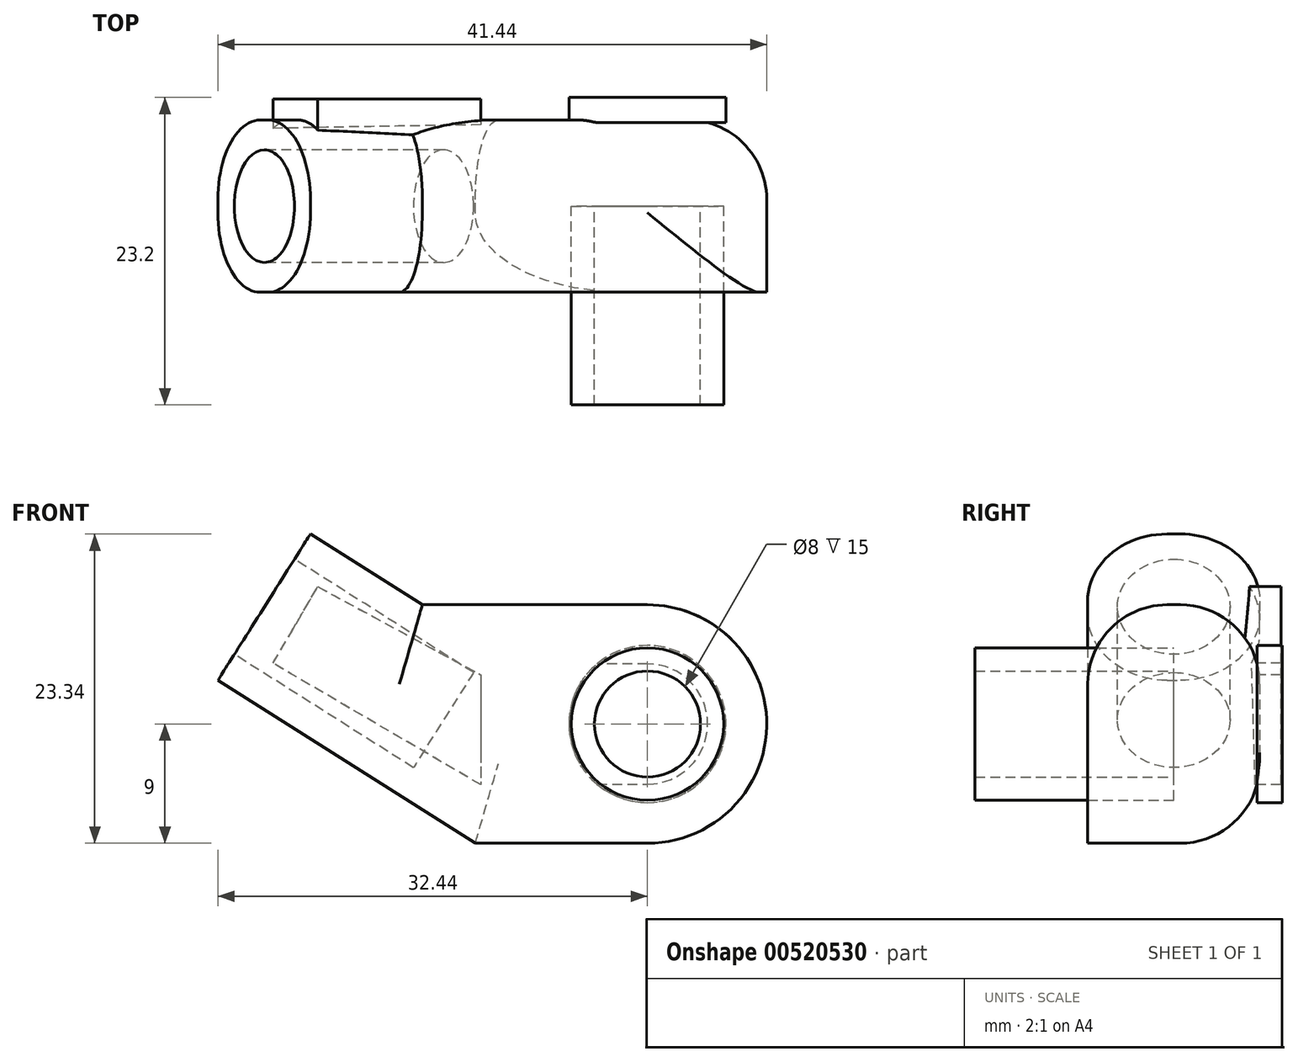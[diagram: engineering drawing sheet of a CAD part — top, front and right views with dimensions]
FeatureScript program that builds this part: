
annotation { "Feature Type Name" : "Feature", "Feature Type Description" : "" }
export const myFeature = defineFeature(function(context is Context, id is Id, definition is map)
    precondition{}
    {
        {
            var Q0;
            Q0=qCreatedBy(makeId("Front.planeOp"),FACE);
            var sketch = newSketch(context, id + "F0", { "sketchPlane" : qUnion([Q0])});
            skCircle(sketch, "E0", {"center": v(0, 0) * mm, "radius": 9 * mm});
            skLineSegment(sketch, "E1", {"start": v(0, -9) * mm, "end": v(-13, -9) * mm});
            skLineSegment(sketch, "E2", {"start": v(-13, -9) * mm, "end": v(-32.44, 3.3) * mm});
            skLineSegment(sketch, "E3", {"start": v(-32.44, 3.3) * mm, "end": v(-25.45, 14.34) * mm});
            skLineSegment(sketch, "E4", {"start": v(-25.45, 14.34) * mm, "end": v(-17, 9) * mm});
            skLineSegment(sketch, "E5", {"start": v(-17, 9) * mm, "end": v(0, 9) * mm});
            skSolve(sketch);
        }
        {
            var Q0;
            {var subQ0=sQuery(id+"F0.wireOp",EDGE,"E1");Q0=makeQuery(id+"F0.imprint","IMPRINT",FACE,{"disambiguationData":[TD([[makeQuery(id+"F0.imprint","IMPRINT",EDGE,{"derivedFrom":subQ0}),-1.0]])]});}
            var Q1;
            {var subQ0=sQuery(id+"F0.wireOp",EDGE,"E0");var subQ1=makeQuery(id+"F0.imprint","INTERSECT",VERTEX,{"derivedFrom":[subQ0,sQuery(id+"F0.wireOp",EDGE,"E1")]});Q1=makeQuery(id+"F0.imprint","IMPRINT",FACE,{"disambiguationData":[TD([[makeQuery(id+"F0.imprint","IMPRINT",EDGE,{"disambiguationData":[TD([[subQ1,1.0]])],"derivedFrom":subQ0}),1.0]])]});}
            extrude(context, id + "F1", {"entities" : qUnion([Q0, Q1]), "endBound" : BoundingType.SYMMETRIC, "depth" : 13 * mm});
        }
        {
            var Q0;
            Q0=makeQuery(id+"F1.opExtrude","SWEPT_FACE",FACE,{"disambiguationData":[OSD([sQuery(id+"F0.wireOp",EDGE,"E3")])]});
            var sketch = newSketch(context, id + "F2", { "sketchPlane" : qUnion([Q0])});
            skCircle(sketch, "E6", {"center": v(0, -7.98) * mm, "radius": 4.25 * mm});
            skSolve(sketch);
        }
        {
            var Q0;
            Q0=qSketchRegion(id+"F2",true);
            extrude(context, id + "F3", {"entities" : qUnion([Q0]), "operationType" : NewBodyOperationType.REMOVE, "oppositeDirection" : true, "depth" : 16 * mm});
        }
        {
            var Q0;
            Q0=makeQuery(id+"F1.opExtrude","CAP_EDGE",EDGE,{"disambiguationData":[OSD([sQuery(id+"F0.wireOp",EDGE,"E4")])],"isStart":true});
            var Q1;
            Q1=makeQuery(id+"F1.opExtrude","CAP_EDGE",EDGE,{"disambiguationData":[OSD([sQuery(id+"F0.wireOp",EDGE,"E5")])],"isStart":true});
            var Q2;
            Q2=makeQuery(id+"F1.opExtrude","CAP_EDGE",EDGE,{"disambiguationData":[OSD([sQuery(id+"F0.wireOp",EDGE,"E2")])],"isStart":true});
            fillet(context, id + "F4", {"entities" : qUnion([Q0, Q1, Q2]), "radius" : 6 * mm, "tangentPropagation" : true, "allowEdgeOverflow" : false});
        }
        {
            var Q0;
            Q0=makeQuery(id+"F1.opExtrude","CAP_EDGE",EDGE,{"disambiguationData":[OSD([sQuery(id+"F0.wireOp",EDGE,"E4")])],"isStart":false});
            var Q1;
            Q1=makeQuery(id+"F1.opExtrude","CAP_EDGE",EDGE,{"disambiguationData":[OSD([sQuery(id+"F0.wireOp",EDGE,"E5")])],"isStart":false});
            var Q2;
            Q2=makeQuery(id+"F1.opExtrude","CAP_EDGE",EDGE,{"disambiguationData":[OSD([sQuery(id+"F0.wireOp",EDGE,"E2")])],"isStart":false});
            fillet(context, id + "F5", {"entities" : qUnion([Q0, Q1, Q2]), "radius" : 6 * mm, "allowEdgeOverflow" : false});
        }
        {
            var Q0;
            Q0=qCreatedBy(makeId("Front.planeOp"),FACE);
            var sketch = newSketch(context, id + "F6", { "sketchPlane" : qUnion([Q0])});
            skCircle(sketch, "E7", {"center": v(0, 0) * mm, "radius": 4 * mm});
            skCircle(sketch, "E8", {"center": v(0, 0) * mm, "radius": 5.75 * mm});
            skSolve(sketch);
        }
        {
            var Q0;
            Q0=makeQuery(id+"F6.imprint","IMPRINT",FACE,{"disambiguationData":[TD([[makeQuery(id+"F6.imprint","IMPRINT",EDGE,{"derivedFrom":sQuery(id+"F6.wireOp",EDGE,"E7")}),-1.0]])]});
            var Q1;
            Q1=sQuery(id+"F6.wireOp",EDGE,"E7");
            var Q2;
            Q2=sQuery(id+"F6.wireOp",EDGE,"E8");
            extrude(context, id + "F7", {"entities" : qUnion([Q0]), "surfaceEntities" : qUnion([Q1, Q2]), "depth" : 15 * mm});
        }
        {
            var Q0;
            Q0=qCreatedBy(makeId("Front.planeOp"),FACE);
            var sketch = newSketch(context, id + "F8", { "sketchPlane" : qUnion([Q0])});
            skCircle(sketch, "E9", {"center": v(0, 0) * mm, "radius": 5.92 * mm});
            skSolve(sketch);
        }
        {
            var Q0;
            Q0 = qSketchRegion(id + "F8", true);
            extrude(context, id + "F9", {"entities" : qUnion([Q0]), "operationType" : NewBodyOperationType.ADD, "oppositeDirection" : true, "depth" : 8.2 * mm, "offsetDistance" : 25 * mm, "hasSecondDirection" : true, "secondDirectionOppositeDirection" : true, "secondDirectionDepth" : 6.3 * mm});
        }
        {
            var Q0;
            Q0=qCreatedBy(makeId("Front.planeOp"),FACE);
            var sketch = newSketch(context, id + "F10", { "sketchPlane" : qUnion([Q0])});
            skLineSegment(sketch, "E10", {"start": v(-12.58, 3.7) * mm, "end": v(-12.58, -4.59) * mm});
            skLineSegment(sketch, "E11", {"start": v(-12.58, -4.59) * mm, "end": v(-28.27, 4.59) * mm});
            skLineSegment(sketch, "E12", {"start": v(-28.27, 4.59) * mm, "end": v(-24.9, 10.37) * mm});
            skLineSegment(sketch, "E13", {"start": v(-24.9, 10.37) * mm, "end": v(-12.58, 3.7) * mm});
            skSolve(sketch);
        }
        {
            var Q0;
            Q0 = qSketchRegion(id + "F10", true);
            extrude(context, id + "F11", {"entities" : qUnion([Q0]), "operationType" : NewBodyOperationType.ADD, "oppositeDirection" : true, "depth" : 8.1 * mm, "offsetDistance" : 25 * mm, "hasSecondDirection" : true, "secondDirectionOppositeDirection" : true, "secondDirectionDepth" : 4.4 * mm});
        }
    });
